# Revit family: Window-Casement-Quaker-C600-Casement_Fixed
name_source: partatom
category: Windows
units: mm (PartAtom-declared; Revit-internal decimal feet)

## family parameters
Always vertical = Yes
Classification Number = 23.30.20.17.21.14
Cut with Voids When Loaded = No
Host = Wall
Room Calculation Point = No
Shared = No

## types (2) — shared parameters
Analytic Construction = <None>
Default Sill Height = 36 "
Frame Material = Powder Coat - Quaker - White
Glass Material = Glass - Quaker - Insulated
Height = 36 "
Installation-Fabrication = https://www.quakercommercialwindows.com
Keynote = 08 51 13
Manufacturer = Quaker Windows & Doors
Rough Height = 36 "
Rough Width = 48 "
Swing Width = 24 "
URL = https://www.quakercommercialwindows.com
Wall Closure = By host
Width = 48 "
to backside of fin = 1.312 "
zero-valued in all types: Cost

## per-type parameters (varying)
| type | Bevel Exterior | Description | Door Swing | Model | Nail Fins | Squared Off Exterior |
| 48" x 36", Bevel Exterior | Yes | Casement Window, Double, Casement - Fixed, Bevel Exterior | Yes | C605 Casement | Yes | No |
| 48" x 36", Squared Off Exterior | No | Casement Window, Double, Casement - Fixed, Squared Off Exterior | No | C600 Casement | No | Yes |

## geometry (parser evidence)
native form markers: Sweep x6
no freeform markers — native parametric forms only
